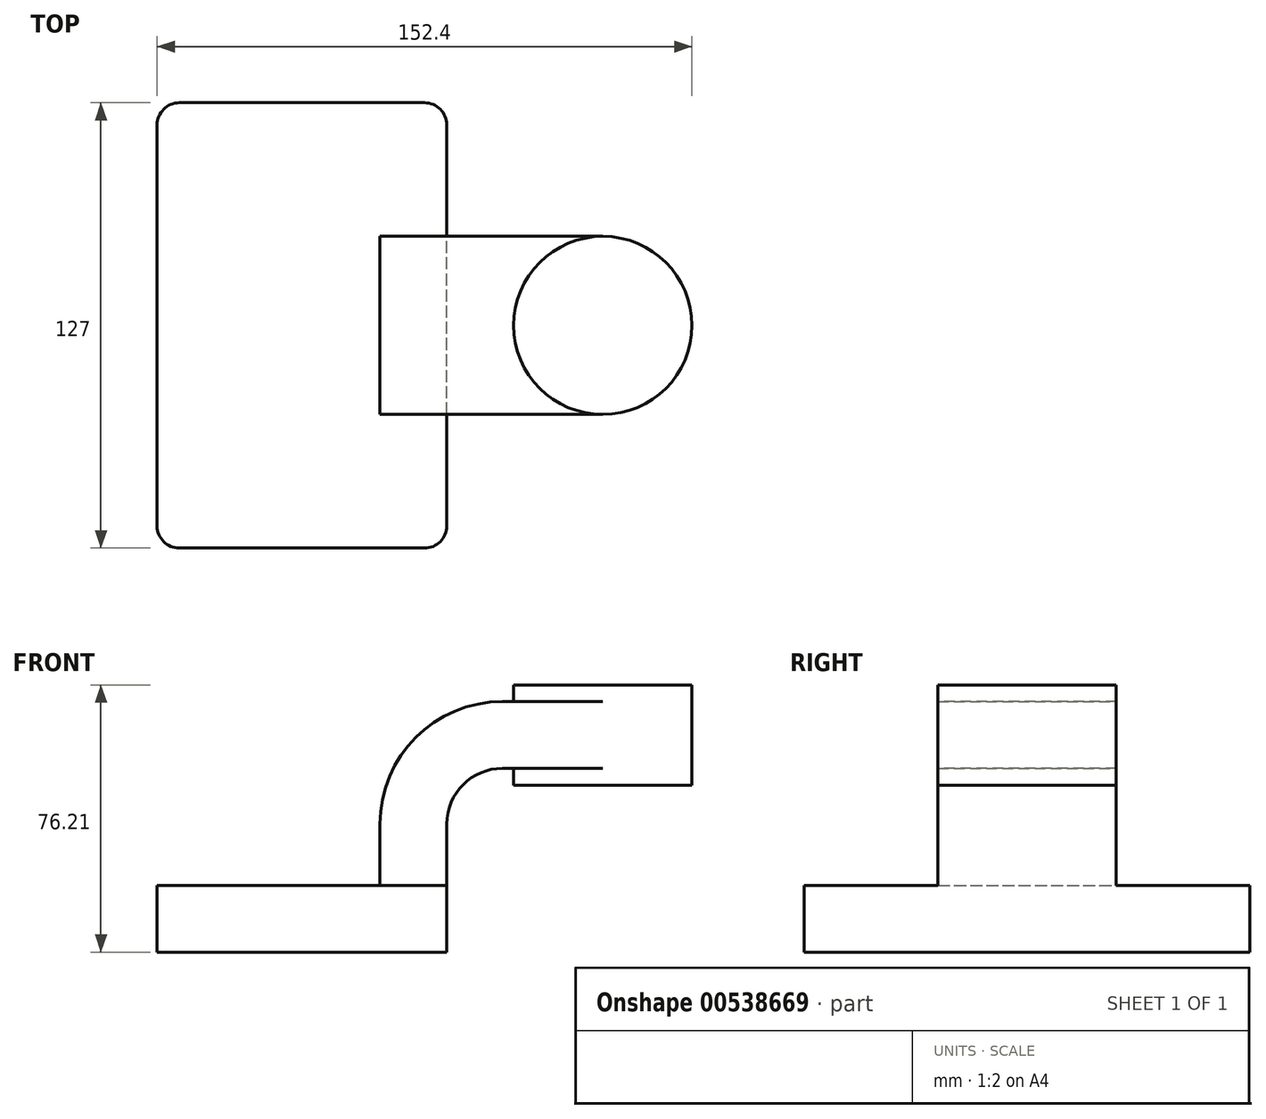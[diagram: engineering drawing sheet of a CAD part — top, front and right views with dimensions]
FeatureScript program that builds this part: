
annotation { "Feature Type Name" : "Feature", "Feature Type Description" : "" }
export const myFeature = defineFeature(function(context is Context, id is Id, definition is map)
    precondition{}
    {
        {
            var Q0;
            Q0=qCreatedBy(makeId("Front.planeOp"),FACE);
            var sketch = newSketch(context, id + "F0", { "sketchPlane" : qUnion([Q0])});
            skLineSegment(sketch, "E0.bottom", {"start": v(-41.28, 9.52) * mm, "end": v(41.28, 9.53) * mm});
            skLineSegment(sketch, "E0.top", {"start": v(-41.28, -9.52) * mm, "end": v(41.28, -9.52) * mm});
            skLineSegment(sketch, "E0.left", {"start": v(-41.28, 9.52) * mm, "end": v(-41.27, -9.53) * mm});
            skLineSegment(sketch, "E0.right", {"start": v(41.28, 9.53) * mm, "end": v(41.28, -9.52) * mm});
            skPoint(sketch, "E0.middle", {"position": v(0, 0) * mm});
            skLineSegment(sketch, "E1.bottom", {"start": v(111.12, 38.1) * mm, "end": v(60.32, 38.1) * mm});
            skLineSegment(sketch, "E1.top", {"start": v(111.12, 66.68) * mm, "end": v(60.32, 66.67) * mm});
            skLineSegment(sketch, "E1.left", {"start": v(111.12, 38.1) * mm, "end": v(111.12, 66.68) * mm});
            skLineSegment(sketch, "E1.right", {"start": v(60.32, 38.1) * mm, "end": v(60.32, 66.67) * mm});
            skPoint(sketch, "E1.middle", {"position": v(85.72, 52.39) * mm});
            skLineSegment(sketch, "E2", {"start": v(41.27, 9.53) * mm, "end": v(41.27, 27) * mm});
            skArc(sketch, "E3", {"start": v(41.27, 27) * mm, "mid": v(45.92, 38.23) * mm, "end": v(57.15, 42.88) * mm});
            skLineSegment(sketch, "E4", {"start": v(57.15, 42.88) * mm, "end": v(85.72, 42.88) * mm});
            skLineSegment(sketch, "E5.0", {"start": v(57.15, 61.93) * mm, "end": v(85.72, 61.93) * mm});
            skArc(sketch, "E5.1", {"start": v(22.22, 27) * mm, "mid": v(32.45, 51.7) * mm, "end": v(57.15, 61.93) * mm});
            skLineSegment(sketch, "E5.2", {"start": v(22.22, 9.53) * mm, "end": v(22.22, 27) * mm});
            skFitSpline(sketch, "E6", {"points": [v(-41.28, 9.52) * mm, v(57.15, 61.93) * mm], "startDerivative": vector(35.58, 95.25) * mm, "endDerivative": vector(133.81, -5.32) * mm});
            skPoint(sketch, "E7.endSnap0", {"position": v(85.72, 66.68) * mm});
            skLineSegment(sketch, "E8", {"start": v(85.72, 61.93) * mm, "end": v(85.72, 42.88) * mm});
            skLineSegment(sketch, "E9", {"start": v(85.72, 66.68) * mm, "end": v(85.72, 38.1) * mm});
            skSolve(sketch);
        }
        {
            var Q0;
            Q0=makeQuery(id+"F0.imprint","IMPRINT",FACE,{"disambiguationData":[TD([[makeQuery(id+"F0.imprint","IMPRINT",EDGE,{"derivedFrom":sQuery(id+"F0.wireOp",EDGE,"E0.top")}),1.0]])]});
            extrude(context, id + "F1", {"entities" : qUnion([Q0]), "endBound" : BoundingType.SYMMETRIC, "depth" : 127 * mm, "offsetDistance" : 25.4 * mm});
        }
        {
            var Q0;
            {var subQ1=sQuery(id+"F0.wireOp",EDGE,"E2");Q0=makeQuery(id+"F0.imprint","IMPRINT",FACE,{"disambiguationData":[TD([[makeQuery(id+"F0.imprint","IMPRINT",EDGE,{"derivedFrom":subQ1}),1.0]])]});}
            var Q1;
            {var subQ0=sQuery(id+"F0.wireOp",EDGE,"E4");var subQ1=sQuery(id+"F0.wireOp",EDGE,"E1.right");var subQ2=makeQuery(id+"F0.imprint","INTERSECT",VERTEX,{"derivedFrom":[subQ1,subQ0]});Q1=makeQuery(id+"F0.imprint","IMPRINT",FACE,{"disambiguationData":[TD([[makeQuery(id+"F0.imprint","IMPRINT",EDGE,{"disambiguationData":[TD([[subQ2,-1.0]])],"derivedFrom":subQ1}),-1.0]])]});}
            extrude(context, id + "F2", {"entities" : qUnion([Q0, Q1]), "operationType" : NewBodyOperationType.ADD, "endBound" : BoundingType.SYMMETRIC, "depth" : 50.8 * mm, "offsetDistance" : 25.4 * mm});
        }
        {
            var Q0;
            Q0=makeQuery(id+"F0.imprint","IMPRINT",FACE,{"disambiguationData":[TD([[makeQuery(id+"F0.imprint","IMPRINT",EDGE,{"derivedFrom":sQuery(id+"F0.wireOp",EDGE,"E5.1")}),1.0]])]});
            extrude(context, id + "F3", {"entities" : qUnion([Q0]), "operationType" : NewBodyOperationType.ADD, "endBound" : BoundingType.SYMMETRIC, "depth" : 15.88 * mm, "offsetDistance" : 25.4 * mm});
        }
        {
            var Q0;
            {var subQ0=sQuery(id+"F0.wireOp",EDGE,"E1.left");Q0=makeQuery(id+"F0.imprint","IMPRINT",FACE,{"disambiguationData":[TD([[makeQuery(id+"F0.imprint","IMPRINT",EDGE,{"derivedFrom":subQ0}),1.0]])]});}
            var Q1;
            Q1=sQuery(id+"F0.wireOp",EDGE,"E9");
            revolve(context, id + "F4", {"operationType" : NewBodyOperationType.ADD, "entities" : qUnion([Q0]), "axis" : qUnion([Q1]), "revolveType" : RevolveType.FULL});
        }
        {
            var Q0;
            Q0=makeQuery(id+"F1.opExtrude","CAP_EDGE",EDGE,{"disambiguationData":[OSD([sQuery(id+"F0.wireOp",EDGE,"E0.right")])],"isStart":false});
            var Q1;
            Q1=makeQuery(id+"F1.opExtrude","CAP_EDGE",EDGE,{"disambiguationData":[OSD([sQuery(id+"F0.wireOp",EDGE,"E0.left")])],"isStart":false});
            var Q2;
            Q2=makeQuery(id+"F1.opExtrude","CAP_EDGE",EDGE,{"disambiguationData":[OSD([sQuery(id+"F0.wireOp",EDGE,"E0.right")])],"isStart":true});
            var Q3;
            Q3=makeQuery(id+"F1.opExtrude","CAP_EDGE",EDGE,{"disambiguationData":[OSD([sQuery(id+"F0.wireOp",EDGE,"E0.left")])],"isStart":true});
            fillet(context, id + "F5", {"entities" : qUnion([Q0, Q1, Q2, Q3]), "radius" : 6.35 * mm, "tangentPropagation" : true, "allowEdgeOverflow" : false});
        }
    });
